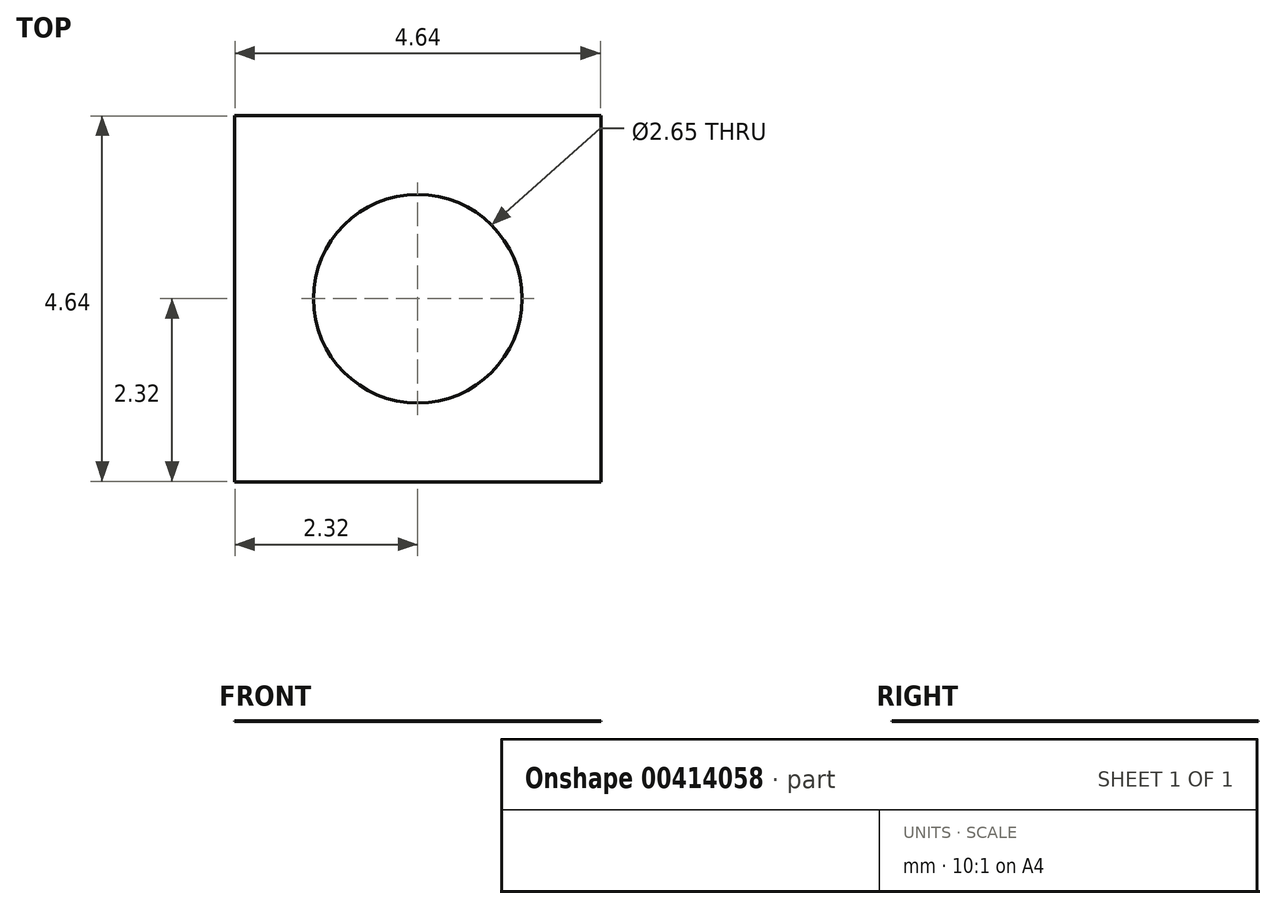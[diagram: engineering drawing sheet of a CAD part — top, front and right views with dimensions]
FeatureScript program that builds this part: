
annotation { "Feature Type Name" : "Feature", "Feature Type Description" : "" }
export const myFeature = defineFeature(function(context is Context, id is Id, definition is map)
    precondition{}
    {
        {
            var Q0;
            Q0=qCreatedBy(makeId("Top.planeOp"),FACE);
            var sketch = newSketch(context, id + "F0", { "sketchPlane" : qUnion([Q0])});
            skLineSegment(sketch, "E0.bottom", {"start": v(2.32, 2.32) * mm, "end": v(-2.32, 2.32) * mm});
            skLineSegment(sketch, "E0.top", {"start": v(2.32, -2.32) * mm, "end": v(-2.32, -2.32) * mm});
            skLineSegment(sketch, "E0.left", {"start": v(2.32, 2.33) * mm, "end": v(2.32, -2.33) * mm});
            skLineSegment(sketch, "E0.right", {"start": v(-2.32, 2.33) * mm, "end": v(-2.32, -2.33) * mm});
            skPoint(sketch, "E0.middle", {"position": v(0, 0) * mm});
            skCircle(sketch, "E1", {"center": v(0, 0) * mm, "radius": 1.32 * mm});
            skSolve(sketch);
        }
        {
            var Q0;
            Q0=makeQuery(id+"F0.imprint","IMPRINT",FACE,{"disambiguationData":[TD([[makeQuery(id+"F0.imprint","IMPRINT",EDGE,{"derivedFrom":sQuery(id+"F0.wireOp",EDGE,"E0.bottom")}),1.0]])]});
            extrude(context, id + "F1", {"entities" : qUnion([Q0]), "depth" : 1 / 203.2 * mm});
        }
    });
